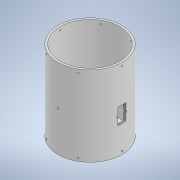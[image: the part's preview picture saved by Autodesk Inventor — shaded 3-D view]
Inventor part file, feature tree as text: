
AUTODESK INVENTOR PART (.ipt)
format: ipt  version: 2022 (Build 260153000, 153)  size: 209,920 bytes
history: native  units: mm
features: extrude x5, sketch x5, plane x4, pattern_circular x1, mirror x1
ambient origin geometry x8: Origin, YZ Plane, XZ Plane, XY Plane, X Axis, Y Axis, Z Axis, Center Point
bodies: Solid1 (feature_tree)
feature tree (16):
  extrude  "Extrusion1"  Depth=40.0mm
  plane  "Work Plane3"
  extrude  "Extrusion9"  [1 undecoded]
  extrude  "Extrusion10"  Depth=5.0mm
  plane  "Work Plane4"
  plane  "Work Plane5"
  extrude  "Extrusion13"  Depth=10.0mm TaperAngle=0.0deg
  pattern_circular  "Circular Pattern1"  [2 undecoded]
  plane  "Work Plane6"
  mirror  "Mirror2"
  extrude  "Extrusion14"  Depth=2.0mm
  sketch  "Sketch1"  dims[d0=37.47mm d1=40.0mm]
  sketch  "Sketch8"  dims[d2=50.0mm d3=0.0mm d34=-21.88mm]
  sketch  "Sketch9"  dims[d35=3.0mm d36=5.0mm]
  sketch  "Sketch13"  dims[d37=2.5mm d40=10.0mm d41=0.0mm]
  sketch  "Sketch14"  dims[d42=3.0mm d43=6.0mm d44=3.0mm d46=18.0mm d47=1.0mm d48=0.0mm d64=0.75mm d65=0.0mm d66=0.0mm d67=60.0mm d68=360.0deg d70=2.0mm d71=0.75mm d72=0.0mm d73=0.0mm d6=0.5mm d7=0.872665mm d8=0.5mm d9=0.872665mm d49=0.5mm d50=0.872665mm]
note: 3 required parameter values undecoded (feature->parameter linkage not recoverable at this tier; creation-order binding heuristic only, values carry confidence <= 0.55)
